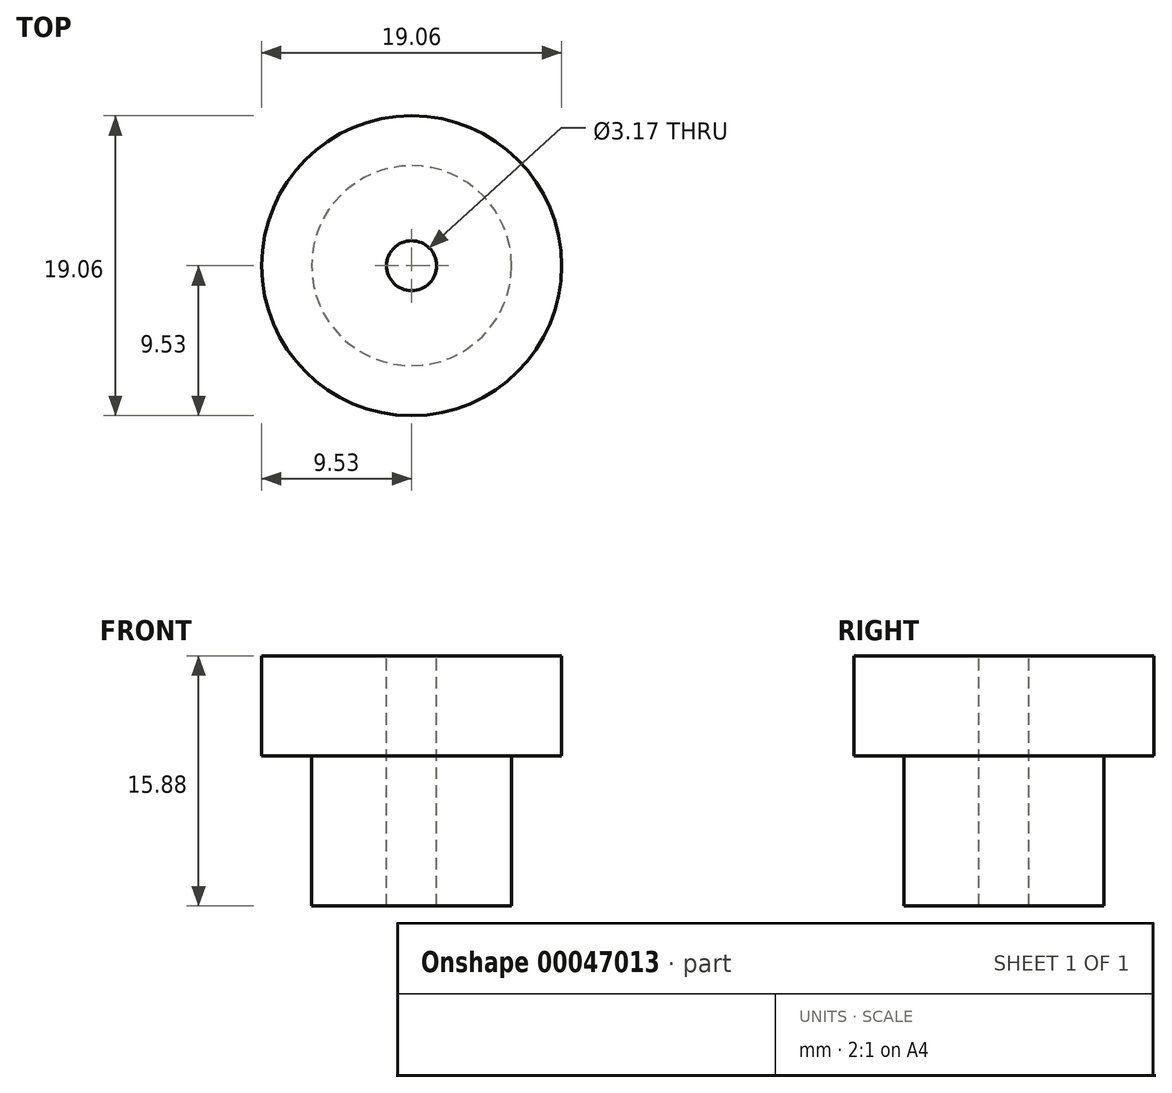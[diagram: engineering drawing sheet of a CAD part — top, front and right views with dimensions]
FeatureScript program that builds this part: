
annotation { "Feature Type Name" : "Feature", "Feature Type Description" : "" }
export const myFeature = defineFeature(function(context is Context, id is Id, definition is map)
    precondition{}
    {
        {
            var Q0;
            Q0=qCreatedBy(makeId("Front.planeOp"),FACE);
            var sketch = newSketch(context, id + "F0", { "sketchPlane" : qUnion([Q0])});
            skLineSegment(sketch, "E0", {"start": v(0, 0) * mm, "end": v(0, 15.88) * mm});
            skLineSegment(sketch, "E1", {"start": v(0, 15.88) * mm, "end": v(-9.53, 15.88) * mm});
            skLineSegment(sketch, "E2", {"start": v(-9.53, 15.87) * mm, "end": v(-9.53, 9.52) * mm});
            skLineSegment(sketch, "E3", {"start": v(-9.53, 9.52) * mm, "end": v(-6.35, 9.53) * mm});
            skLineSegment(sketch, "E4", {"start": v(-6.35, 9.53) * mm, "end": v(-6.35, 0) * mm});
            skLineSegment(sketch, "E5", {"start": v(-6.35, 0) * mm, "end": v(0, 0) * mm});
            skSolve(sketch);
        }
        {
            var Q0;
            Q0=makeQuery(id+"F0.imprint","IMPRINT",FACE,{"disambiguationData":[TD([[makeQuery(id+"F0.imprint","IMPRINT",EDGE,{"derivedFrom":sQuery(id+"F0.wireOp",EDGE,"E0")}),1.0]])]});
            var Q1;
            Q1=sQuery(id+"F0.wireOp",EDGE,"E0");
            revolve(context, id + "F1", {"entities" : qUnion([Q0]), "axis" : qUnion([Q1]), "revolveType" : RevolveType.FULL});
        }
        {
            var Q0;
            Q0=makeQuery(id+"F1.opRevolve","SWEPT_FACE",FACE,{"disambiguationData":[OSD([sQuery(id+"F0.wireOp",EDGE,"E1")])]});
            var sketch = newSketch(context, id + "F2", { "sketchPlane" : qUnion([Q0])});
            skCircle(sketch, "E6.0.0", {"center": v(0, 0) * mm, "radius": 9.53 * mm});
            skCircle(sketch, "E7", {"center": v(0, 0) * mm, "radius": 1.59 * mm});
            skSolve(sketch);
        }
        {
            var Q0;
            Q0=sQuery(id+"F2.wireOp",VERTEX,"E7.center");
            var Q1;
            Q1=makeQuery(id+"F1.opRevolve","SWEPT_BODY",BODY,{"disambiguationData":[OSD([sQuery(id+"F0.wireOp",EDGE,"E0"),sQuery(id+"F0.wireOp",EDGE,"E1"),sQuery(id+"F0.wireOp",EDGE,"E2"),sQuery(id+"F0.wireOp",EDGE,"E3"),sQuery(id+"F0.wireOp",EDGE,"E4"),sQuery(id+"F0.wireOp",EDGE,"E5")])]});
            hole(context, id + "F3", {"style" : HoleStyle.SIMPLE, "holeDiameter" : 3.17 * mm, "endStyle" : HoleEndStyle.THROUGH, "locations" : qUnion([Q0]), "scope" : qUnion([Q1])});
        }
    });
